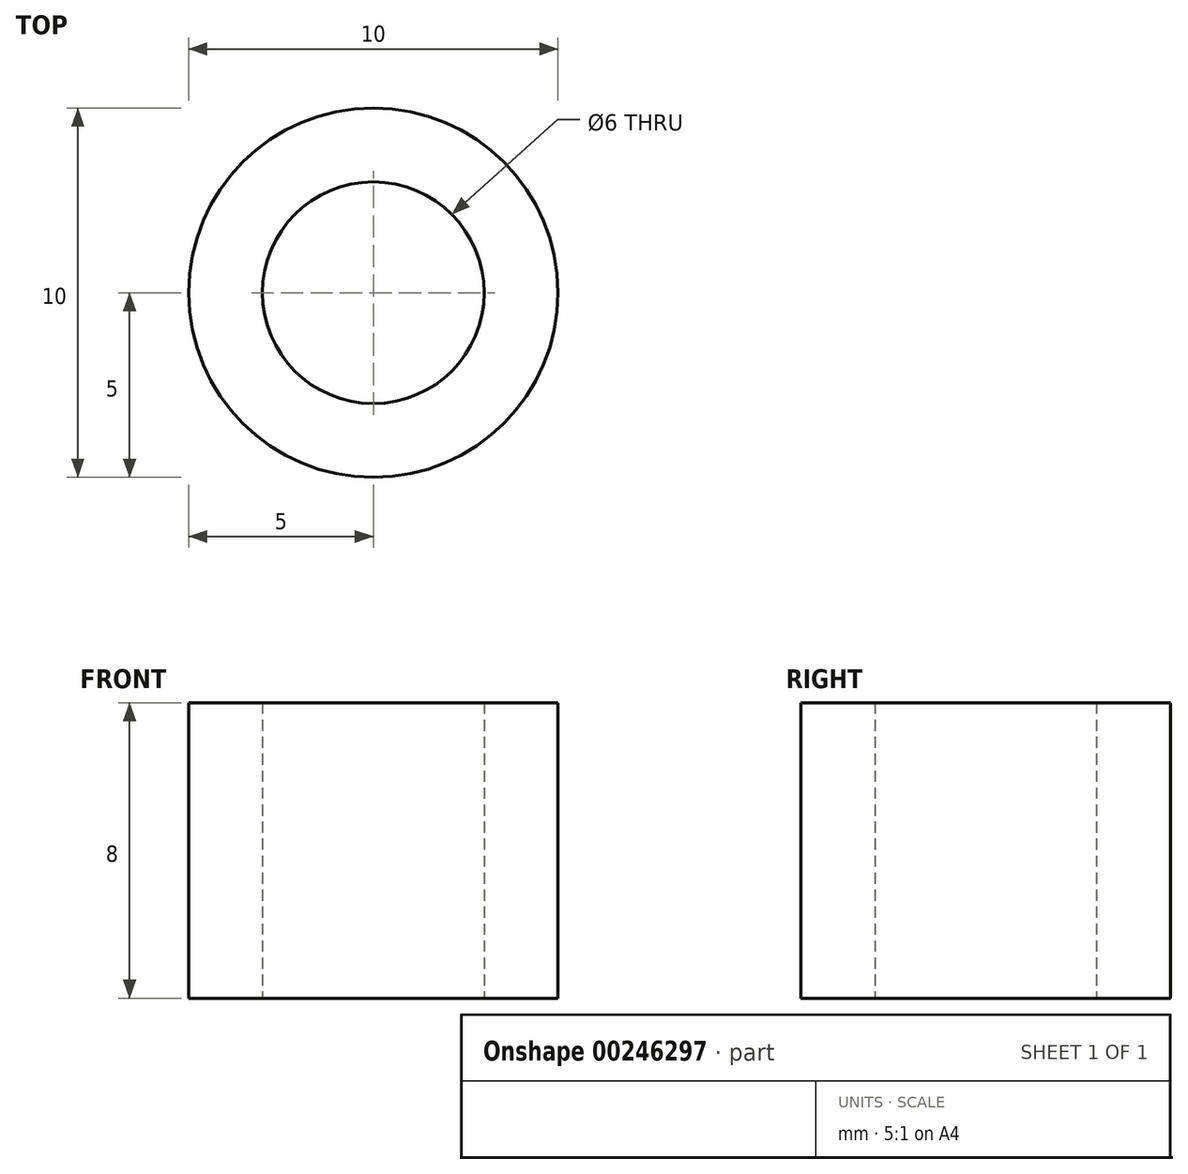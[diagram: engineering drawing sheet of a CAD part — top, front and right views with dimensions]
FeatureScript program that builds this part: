
annotation { "Feature Type Name" : "Feature", "Feature Type Description" : "" }
export const myFeature = defineFeature(function(context is Context, id is Id, definition is map)
    precondition{}
    {
        {
            var Q0;
            Q0=qCreatedBy(makeId("Top.planeOp"),FACE);
            var sketch = newSketch(context, id + "F0", { "sketchPlane" : qUnion([Q0])});
            skCircle(sketch, "E0", {"center": v(0, 0) * mm, "radius": 3 * mm});
            skCircle(sketch, "E1", {"center": v(0, 0) * mm, "radius": 5 * mm});
            skSolve(sketch);
        }
        {
            var Q0;
            Q0 = qSketchRegion(id + "F0", true);
            extrude(context, id + "F1", {"entities" : qUnion([Q0]), "depth" : 8 * mm});
        }
    });
